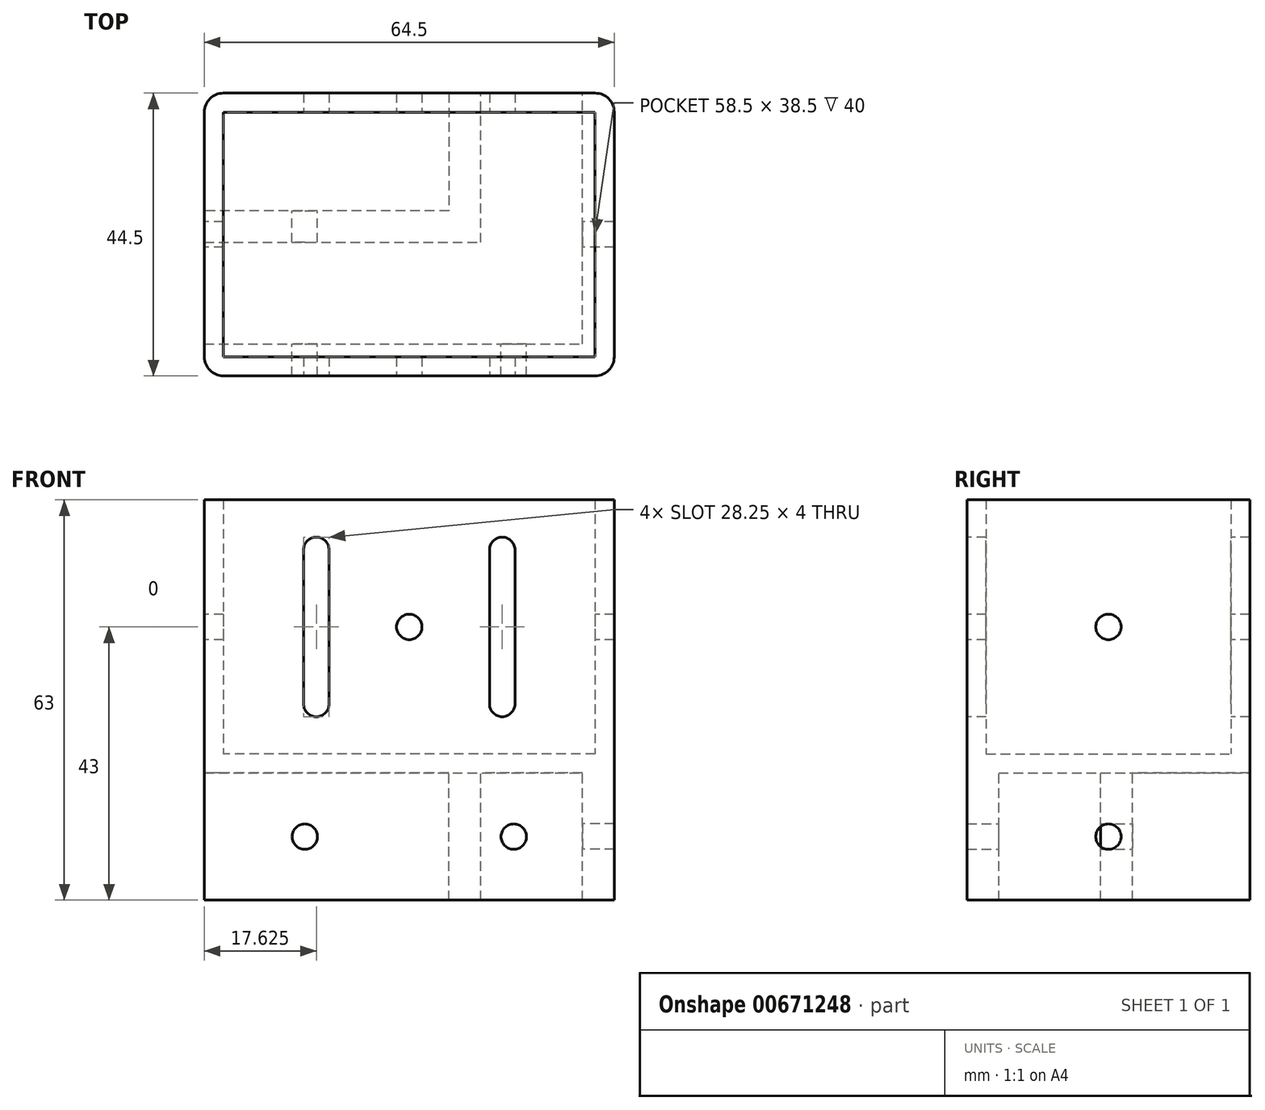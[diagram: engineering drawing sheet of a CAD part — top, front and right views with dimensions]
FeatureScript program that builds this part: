
annotation { "Feature Type Name" : "Feature", "Feature Type Description" : "" }
export const myFeature = defineFeature(function(context is Context, id is Id, definition is map)
    precondition{}
    {
        {
            var Q0;
            Q0=qCreatedBy(makeId("Top.planeOp"),FACE);
            var sketch = newSketch(context, id + "F0", { "sketchPlane" : qUnion([Q0])});
            skLineSegment(sketch, "E0.bottom", {"start": v(32.25, -22.25) * mm, "end": v(-32.25, -22.25) * mm});
            skLineSegment(sketch, "E0.top", {"start": v(32.25, 22.25) * mm, "end": v(-32.25, 22.25) * mm});
            skLineSegment(sketch, "E0.left", {"start": v(32.25, -22.25) * mm, "end": v(32.25, 22.25) * mm});
            skLineSegment(sketch, "E0.right", {"start": v(-32.25, -22.25) * mm, "end": v(-32.25, 22.25) * mm});
            skPoint(sketch, "E0.middle", {"position": v(0, 0) * mm});
            skLineSegment(sketch, "E1.bottom", {"start": v(29.25, -19.25) * mm, "end": v(-29.25, -19.25) * mm});
            skLineSegment(sketch, "E1.top", {"start": v(29.25, 19.25) * mm, "end": v(-29.25, 19.25) * mm});
            skLineSegment(sketch, "E1.left", {"start": v(29.25, -19.25) * mm, "end": v(29.25, 19.25) * mm});
            skLineSegment(sketch, "E1.right", {"start": v(-29.25, -19.25) * mm, "end": v(-29.25, 19.25) * mm});
            skSolve(sketch);
        }
        {
            var Q0;
            Q0=makeQuery(id+"F0.imprint","IMPRINT",FACE,{"disambiguationData":[TD([[makeQuery(id+"F0.imprint","IMPRINT",EDGE,{"derivedFrom":sQuery(id+"F0.wireOp",EDGE,"E0.bottom")}),-1.0]])]});
            extrude(context, id + "F1", {"entities" : qUnion([Q0]), "depth" : 40 * mm, "offsetDistance" : 25 * mm});
        }
        {
            var Q0;
            Q0=makeQuery(id+"F0.imprint","IMPRINT",FACE,{"disambiguationData":[TD([[makeQuery(id+"F0.imprint","IMPRINT",EDGE,{"derivedFrom":sQuery(id+"F0.wireOp",EDGE,"E1.bottom")}),-1.0]])]});
            var Q1;
            Q1=makeQuery(id+"F0.imprint","IMPRINT",FACE,{"disambiguationData":[TD([[makeQuery(id+"F0.imprint","IMPRINT",EDGE,{"derivedFrom":sQuery(id+"F0.wireOp",EDGE,"E0.bottom")}),-1.0]])]});
            extrude(context, id + "F2", {"entities" : qUnion([Q0, Q1]), "operationType" : NewBodyOperationType.ADD, "depth" : -3 * mm, "offsetDistance" : 25 * mm});
        }
        {
            var Q0;
            Q0=makeQuery(id+"F2.opExtrude","CAP_FACE",FACE,{"disambiguationData":[OSD([sQuery(id+"F0.wireOp",EDGE,"E0.bottom"),sQuery(id+"F0.wireOp",EDGE,"E0.top"),sQuery(id+"F0.wireOp",EDGE,"E0.left"),sQuery(id+"F0.wireOp",EDGE,"E0.right")])],"isStart":false});
            var sketch = newSketch(context, id + "F3", { "sketchPlane" : qUnion([Q0])});
            skLineSegment(sketch, "E2.0", {"start": v(32.25, -22.25) * mm, "end": v(27.25, -22.25) * mm});
            skLineSegment(sketch, "E3.0", {"start": v(-32.25, 22.25) * mm, "end": v(-32.25, 17.25) * mm});
            skLineSegment(sketch, "E4.0", {"start": v(32.25, 22.25) * mm, "end": v(-32.25, 22.25) * mm});
            skLineSegment(sketch, "E5.0", {"start": v(32.25, 22.25) * mm, "end": v(32.25, -22.25) * mm});
            skLineSegment(sketch, "E6", {"start": v(32.25, -22.25) * mm, "end": v(32.25, 22.25) * mm});
            skLineSegment(sketch, "E7", {"start": v(-32.25, 17.25) * mm, "end": v(27.25, 17.25) * mm});
            skLineSegment(sketch, "E8", {"start": v(27.25, 17.25) * mm, "end": v(27.25, -22.25) * mm});
            skLineSegment(sketch, "E9", {"start": v(27.25, -22.25) * mm, "end": v(32.25, -22.25) * mm});
            skPoint(sketch, "E10.orphan", {"position": v(-32.25, -22.25) * mm});
            skLineSegment(sketch, "E11", {"start": v(-32.25, 1.25) * mm, "end": v(11.25, 1.25) * mm});
            skLineSegment(sketch, "E12", {"start": v(11.25, 1.25) * mm, "end": v(11.25, -22.25) * mm});
            skLineSegment(sketch, "E13", {"start": v(11.25, -22.25) * mm, "end": v(6.25, -22.25) * mm});
            skLineSegment(sketch, "E14", {"start": v(6.25, -22.25) * mm, "end": v(6.25, -3.75) * mm});
            skLineSegment(sketch, "E15", {"start": v(6.25, -3.75) * mm, "end": v(-32.25, -3.75) * mm});
            skLineSegment(sketch, "E16", {"start": v(-32.25, -3.75) * mm, "end": v(-32.25, 1.25) * mm});
            skSolve(sketch);
        }
        {
            var Q0;
            Q0 = qSketchRegion(id + "F3", true);
            extrude(context, id + "F4", {"entities" : qUnion([Q0]), "operationType" : NewBodyOperationType.ADD, "depth" : 20 * mm, "offsetDistance" : 25 * mm});
        }
        {
            var Q0;
            Q0=makeQuery(id+"F1.opExtrude","SWEPT_FACE",FACE,{"disambiguationData":[OSD([sQuery(id+"F0.wireOp",EDGE,"E1.top")])]});
            var sketch = newSketch(context, id + "F5", { "sketchPlane" : qUnion([Q0])});
            skLineSegment(sketch, "E17.0.0", {"start": v(-29.25, 0) * mm, "end": v(29.25, 0) * mm, "construction": true});
            skLineSegment(sketch, "E17.0.1", {"start": v(29.25, 0) * mm, "end": v(29.25, 40) * mm, "construction": true});
            skLineSegment(sketch, "E17.0.2", {"start": v(29.25, 40) * mm, "end": v(-29.25, 40) * mm, "construction": true});
            skLineSegment(sketch, "E17.0.3", {"start": v(-29.25, 40) * mm, "end": v(-29.25, 0) * mm, "construction": true});
            skLineSegment(sketch, "E18.bottom", {"start": v(14.63, 5.87) * mm, "end": v(14.62, 5.87) * mm});
            skLineSegment(sketch, "E18.top", {"start": v(14.63, 34.13) * mm, "end": v(14.62, 34.13) * mm});
            skLineSegment(sketch, "E18.left", {"start": v(16.62, 7.87) * mm, "end": v(16.62, 32.13) * mm});
            skLineSegment(sketch, "E18.right", {"start": v(12.63, 7.87) * mm, "end": v(12.63, 32.13) * mm});
            skPoint(sketch, "E19.visualSharp", {"position": v(16.62, 5.87) * mm});
            skArc(sketch, "E19.filletArc", {"start": v(14.63, 5.87) * mm, "mid": v(16.04, 6.46) * mm, "end": v(16.63, 7.87) * mm});
            skPoint(sketch, "E20.visualSharp", {"position": v(12.63, 5.87) * mm});
            skArc(sketch, "E20.filletArc", {"start": v(12.62, 7.87) * mm, "mid": v(13.21, 6.46) * mm, "end": v(14.62, 5.87) * mm});
            skPoint(sketch, "E21.visualSharp", {"position": v(16.62, 34.13) * mm});
            skArc(sketch, "E21.filletArc", {"start": v(16.62, 32.13) * mm, "mid": v(16.04, 33.54) * mm, "end": v(14.63, 34.13) * mm});
            skPoint(sketch, "E22.visualSharp", {"position": v(12.63, 34.13) * mm});
            skArc(sketch, "E22.filletArc", {"start": v(14.62, 34.13) * mm, "mid": v(13.21, 33.54) * mm, "end": v(12.62, 32.13) * mm});
            skLineSegment(sketch, "E23", {"start": v(14.63, 5.87) * mm, "end": v(14.63, 0) * mm, "construction": true});
            skLineSegment(sketch, "E24", {"start": v(14.63, 34.13) * mm, "end": v(14.63, 40) * mm, "construction": true});
            skLineSegment(sketch, "E25", {"start": v(29.25, 20) * mm, "end": v(16.62, 20) * mm, "construction": true});
            skLineSegment(sketch, "E26", {"start": v(12.63, 20) * mm, "end": v(0, 20) * mm, "construction": true});
            skArc(sketch, "E27.MirrorCS", {"start": v(-14.62, 34.13) * mm, "mid": v(-13.21, 33.54) * mm, "end": v(-12.62, 32.13) * mm});
            skArc(sketch, "E28.MirrorCS", {"start": v(-16.63, 32.13) * mm, "mid": v(-16.04, 33.54) * mm, "end": v(-14.63, 34.13) * mm});
            skLineSegment(sketch, "E29.MirrorCS", {"start": v(-16.62, 7.87) * mm, "end": v(-16.62, 32.13) * mm});
            skLineSegment(sketch, "E30.MirrorCS", {"start": v(-12.63, 7.87) * mm, "end": v(-12.63, 32.13) * mm});
            skArc(sketch, "E31.MirrorCS", {"start": v(-12.63, 7.87) * mm, "mid": v(-13.21, 6.46) * mm, "end": v(-14.63, 5.87) * mm});
            skArc(sketch, "E32.MirrorCS", {"start": v(-14.63, 5.87) * mm, "mid": v(-16.04, 6.46) * mm, "end": v(-16.63, 7.87) * mm});
            skCircle(sketch, "E33", {"center": v(0, 20) * mm, "radius": 2 * mm});
            skSolve(sketch);
        }
        {
            var Q0;
            Q0 = qSketchRegion(id + "F5", true);
            var Q1;
            {var subQ0=sQuery(id+"F0.wireOp",EDGE,"E0.bottom");Q1=makeQuery(id+"F4.boolean.opBoolean","MERGE",FACE,{"derivedFrom":[makeQuery(id+"F2.boolean.opBoolean","MERGE",FACE,{"derivedFrom":[makeQuery(id+"F1.opExtrude","SWEPT_FACE",FACE,{"disambiguationData":[OSD([subQ0])]}),makeQuery(id+"F2.opExtrude","SWEPT_FACE",FACE,{"disambiguationData":[OSD([subQ0])]})]}),makeQuery(id+"F4.opExtrude","SWEPT_FACE",FACE,{"disambiguationData":[OSD([sQuery(id+"F3.wireOp",EDGE,"E4.0")])]})]});}
            extrude(context, id + "F6", {"entities" : qUnion([Q0]), "operationType" : NewBodyOperationType.REMOVE, "endBound" : BoundingType.THROUGH_ALL, "oppositeDirection" : true, "depth" : 25 * mm, "offsetDistance" : 25 * mm, "hasSecondDirection" : true, "secondDirectionBound" : SecondDirectionBoundingType.UP_TO_SURFACE, "secondDirectionOppositeDirection" : false, "secondDirectionDepth" : 25 * mm, "secondDirectionBoundEntityFace" : qUnion([Q1])});
        }
        {
            var Q0;
            {var subQ0=sQuery(id+"F0.wireOp",EDGE,"E0.right");var subQ1=sQuery(id+"F0.wireOp",EDGE,"E0.top");Q0=makeQuery(id+"F2.boolean.opBoolean","MERGE",EDGE,{"derivedFrom":[makeQuery(id+"F1.opExtrude","SWEPT_EDGE",EDGE,{"disambiguationData":[OSD([subQ1,subQ0])]}),makeQuery(id+"F2.opExtrude","SWEPT_EDGE",EDGE,{"disambiguationData":[OSD([subQ1,subQ0])]})]});}
            var Q1;
            {var subQ0=sQuery(id+"F0.wireOp",EDGE,"E0.right");var subQ1=sQuery(id+"F0.wireOp",EDGE,"E0.bottom");Q1=makeQuery(id+"F4.boolean.opBoolean","MERGE",EDGE,{"derivedFrom":[makeQuery(id+"F2.boolean.opBoolean","MERGE",EDGE,{"derivedFrom":[makeQuery(id+"F1.opExtrude","SWEPT_EDGE",EDGE,{"disambiguationData":[OSD([subQ1,subQ0])]}),makeQuery(id+"F2.opExtrude","SWEPT_EDGE",EDGE,{"disambiguationData":[OSD([subQ1,subQ0])]})]}),makeQuery(id+"F4.opExtrude","SWEPT_EDGE",EDGE,{"disambiguationData":[OSD([sQuery(id+"F3.wireOp",EDGE,"E4.0"),sQuery(id+"F3.wireOp",EDGE,"E3.0")])]})]});}
            var Q2;
            {var subQ0=sQuery(id+"F0.wireOp",EDGE,"E0.left");var subQ1=sQuery(id+"F0.wireOp",EDGE,"E0.top");Q2=makeQuery(id+"F4.boolean.opBoolean","MERGE",EDGE,{"derivedFrom":[makeQuery(id+"F2.boolean.opBoolean","MERGE",EDGE,{"derivedFrom":[makeQuery(id+"F1.opExtrude","SWEPT_EDGE",EDGE,{"disambiguationData":[OSD([subQ1,subQ0])]}),makeQuery(id+"F2.opExtrude","SWEPT_EDGE",EDGE,{"disambiguationData":[OSD([subQ1,subQ0])]})]}),makeQuery(id+"F4.opExtrude","SWEPT_EDGE",EDGE,{"disambiguationData":[OSD([sQuery(id+"F3.wireOp",EDGE,"E6"),sQuery(id+"F3.wireOp",EDGE,"E9")])]})]});}
            var Q3;
            {var subQ0=sQuery(id+"F0.wireOp",EDGE,"E0.left");var subQ1=sQuery(id+"F0.wireOp",EDGE,"E0.bottom");Q3=makeQuery(id+"F4.boolean.opBoolean","MERGE",EDGE,{"derivedFrom":[makeQuery(id+"F2.boolean.opBoolean","MERGE",EDGE,{"derivedFrom":[makeQuery(id+"F1.opExtrude","SWEPT_EDGE",EDGE,{"disambiguationData":[OSD([subQ1,subQ0])]}),makeQuery(id+"F2.opExtrude","SWEPT_EDGE",EDGE,{"disambiguationData":[OSD([subQ1,subQ0])]})]}),makeQuery(id+"F4.opExtrude","SWEPT_EDGE",EDGE,{"disambiguationData":[OSD([sQuery(id+"F3.wireOp",EDGE,"E4.0"),sQuery(id+"F3.wireOp",EDGE,"E6")])]})]});}
            fillet(context, id + "F7", {"entities" : qUnion([Q0, Q1, Q2, Q3]), "radius" : 3 * mm, "tangentPropagation" : true, "allowEdgeOverflow" : false});
        }
        {
            var Q0;
            Q0=makeQuery(id+"F4.opExtrude","SWEPT_FACE",FACE,{"disambiguationData":[OSD([sQuery(id+"F3.wireOp",EDGE,"E7")])]});
            var sketch = newSketch(context, id + "F8", { "sketchPlane" : qUnion([Q0])});
            skCircle(sketch, "E34", {"center": v(16.44, -13) * mm, "radius": 2 * mm});
            skCircle(sketch, "E35.MirrorC", {"center": v(-16.44, -13) * mm, "radius": 2 * mm});
            skLineSegment(sketch, "E36", {"start": v(16.44, -13) * mm, "end": v(16.44, -23) * mm, "construction": true});
            skLineSegment(sketch, "E37", {"start": v(16.44, -13) * mm, "end": v(16.44, -3) * mm, "construction": true});
            skSolve(sketch);
        }
        {
            var Q0;
            Q0 = qSketchRegion(id + "F8", true);
            extrude(context, id + "F9", {"entities" : qUnion([Q0]), "operationType" : NewBodyOperationType.REMOVE, "endBound" : BoundingType.SYMMETRIC, "oppositeDirection" : true, "depth" : 50 * mm, "offsetDistance" : 25 * mm});
        }
        {
            var Q0;
            Q0=makeQuery(id+"F4.opExtrude","SWEPT_FACE",FACE,{"disambiguationData":[OSD([sQuery(id+"F3.wireOp",EDGE,"E8")])]});
            var sketch = newSketch(context, id + "F10", { "sketchPlane" : qUnion([Q0])});
            skCircle(sketch, "E38", {"center": v(0, -13) * mm, "radius": 2 * mm});
            skLineSegment(sketch, "E39", {"start": v(0, -13) * mm, "end": v(0, -23) * mm, "construction": true});
            skLineSegment(sketch, "E40", {"start": v(0, -13) * mm, "end": v(0, -3) * mm, "construction": true});
            skSolve(sketch);
        }
        {
            var Q0;
            Q0 = qSketchRegion(id + "F10", true);
            extrude(context, id + "F11", {"entities" : qUnion([Q0]), "operationType" : NewBodyOperationType.REMOVE, "oppositeDirection" : true, "depth" : 25 * mm, "offsetDistance" : 25 * mm});
        }
        {
            var Q0;
            {var subQ0=sQuery(id+"F0.wireOp",EDGE,"E0.right");Q0=makeQuery(id+"F4.boolean.opBoolean","MERGE",FACE,{"derivedFrom":[makeQuery(id+"F2.boolean.opBoolean","MERGE",FACE,{"derivedFrom":[makeQuery(id+"F1.opExtrude","SWEPT_FACE",FACE,{"disambiguationData":[OSD([subQ0])]}),makeQuery(id+"F2.opExtrude","SWEPT_FACE",FACE,{"disambiguationData":[OSD([subQ0])]})]}),makeQuery(id+"F4.opExtrude","SWEPT_FACE",FACE,{"disambiguationData":[OSD([sQuery(id+"F3.wireOp",EDGE,"E3.0")])]})]});}
            var sketch = newSketch(context, id + "F12", { "sketchPlane" : qUnion([Q0])});
            skCircle(sketch, "E41", {"center": v(0, 20) * mm, "radius": 2 * mm});
            skLineSegment(sketch, "E42", {"start": v(0, 0) * mm, "end": v(0, 20) * mm, "construction": true});
            skLineSegment(sketch, "E43", {"start": v(0, 20) * mm, "end": v(0, 40) * mm, "construction": true});
            skSolve(sketch);
        }
        {
            var Q0;
            Q0 = qSketchRegion(id + "F12", true);
            extrude(context, id + "F13", {"entities" : qUnion([Q0]), "operationType" : NewBodyOperationType.REMOVE, "endBound" : BoundingType.THROUGH_ALL, "oppositeDirection" : true, "depth" : 25 * mm, "offsetDistance" : 25 * mm});
        }
    });
